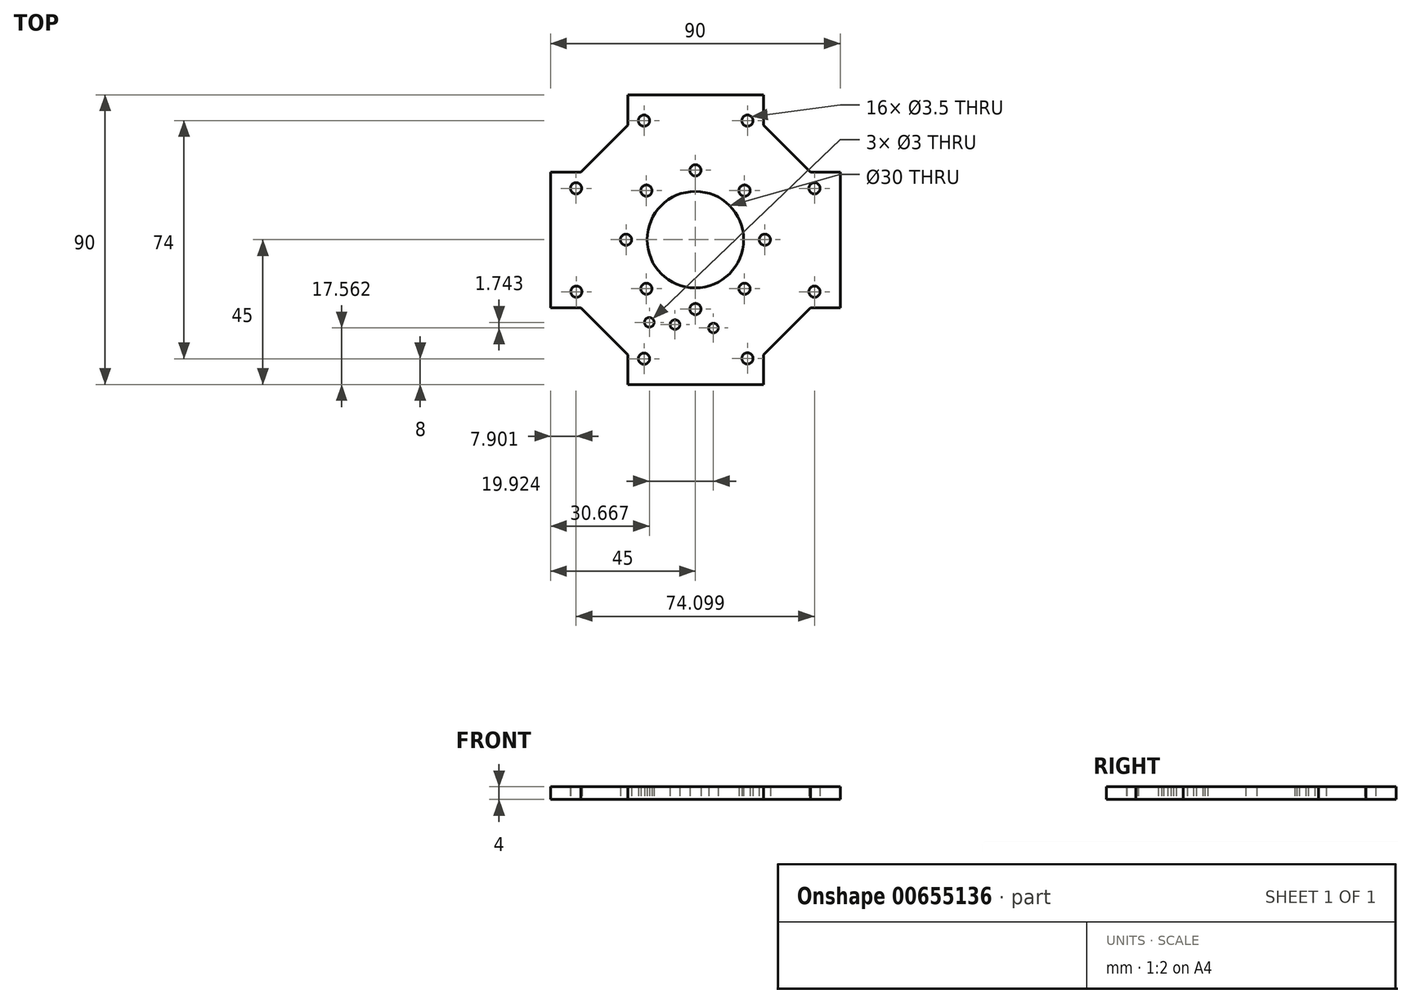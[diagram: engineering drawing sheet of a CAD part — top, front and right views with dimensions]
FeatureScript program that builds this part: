
annotation { "Feature Type Name" : "Feature", "Feature Type Description" : "" }
export const myFeature = defineFeature(function(context is Context, id is Id, definition is map)
    precondition{}
    {
        {
            var Q0;
            Q0=qCreatedBy(makeId("Top.planeOp"),FACE);
            var sketch = newSketch(context, id + "F0", { "sketchPlane" : qUnion([Q0])});
            skLineSegment(sketch, "E0.bottom", {"start": v(24.03, 0) * mm, "end": v(36.03, 0) * mm});
            skLineSegment(sketch, "E0.top", {"start": v(24.03, 90) * mm, "end": v(36.03, 90) * mm});
            skLineSegment(sketch, "E0.left", {"start": v(0, 23.83) * mm, "end": v(0, 35.83) * mm});
            skLineSegment(sketch, "E0.right", {"start": v(90, 23.83) * mm, "end": v(90, 35.83) * mm});
            skLineSegment(sketch, "E1.right", {"start": v(66.17, 80.6) * mm, "end": v(80.8, 65.97) * mm});
            skLineSegment(sketch, "E2", {"start": v(9.4, 65.97) * mm, "end": v(0, 65.97) * mm});
            skLineSegment(sketch, "E3", {"start": v(9.4, 23.83) * mm, "end": v(0, 23.83) * mm});
            skLineSegment(sketch, "E4", {"start": v(24.03, 9.2) * mm, "end": v(24.03, 0) * mm});
            skLineSegment(sketch, "E5", {"start": v(66.17, 9.2) * mm, "end": v(66.17, 0) * mm});
            skLineSegment(sketch, "E6", {"start": v(80.8, 23.83) * mm, "end": v(90, 23.83) * mm});
            skLineSegment(sketch, "E7", {"start": v(80.8, 65.97) * mm, "end": v(90, 65.97) * mm});
            skLineSegment(sketch, "E8", {"start": v(24.03, 80.6) * mm, "end": v(24.03, 90) * mm});
            skLineSegment(sketch, "E9", {"start": v(66.17, 80.6) * mm, "end": v(66.17, 90) * mm});
            skLineSegment(sketch, "E10.trimOffspring", {"start": v(9.4, 23.83) * mm, "end": v(24.03, 9.2) * mm});
            skLineSegment(sketch, "E11.trimOffspring", {"start": v(9.4, 65.97) * mm, "end": v(24.03, 80.6) * mm});
            skPoint(sketch, "E12.orphan", {"position": v(0, 0) * mm});
            skCircle(sketch, "E13", {"center": v(29.03, 82) * mm, "radius": 1.75 * mm});
            skCircle(sketch, "E14", {"center": v(61.17, 82) * mm, "radius": 1.75 * mm});
            skCircle(sketch, "E15", {"center": v(7.9, 60.97) * mm, "radius": 1.75 * mm});
            skCircle(sketch, "E16", {"center": v(8, 28.83) * mm, "radius": 1.75 * mm});
            skCircle(sketch, "E17", {"center": v(82, 28.83) * mm, "radius": 1.75 * mm});
            skCircle(sketch, "E18", {"center": v(29.03, 8) * mm, "radius": 1.75 * mm});
            skCircle(sketch, "E19", {"center": v(61.17, 8.1) * mm, "radius": 1.75 * mm});
            skCircle(sketch, "E20", {"center": v(82, 60.97) * mm, "radius": 1.75 * mm});
            skPoint(sketch, "E21", {"position": v(45, 45) * mm});
            skCircle(sketch, "E22", {"center": v(45, 45) * mm, "radius": 15 * mm});
            skCircle(sketch, "E23", {"center": v(23.43, 45) * mm, "radius": 1.75 * mm});
            skCircle(sketch, "E24", {"center": v(45, 66.57) * mm, "radius": 1.75 * mm});
            skCircle(sketch, "E25", {"center": v(66.57, 45) * mm, "radius": 1.75 * mm});
            skCircle(sketch, "E26", {"center": v(45, 23.43) * mm, "radius": 1.75 * mm});
            skLineSegment(sketch, "E27.trimOffspring", {"start": v(54.17, 90) * mm, "end": v(66.17, 90) * mm});
            skLineSegment(sketch, "E28.trimOffspring", {"start": v(90, 53.97) * mm, "end": v(90, 65.97) * mm});
            skLineSegment(sketch, "E29.trimOffspring", {"start": v(54.17, 0) * mm, "end": v(66.17, 0) * mm});
            skLineSegment(sketch, "E30.trimOffspring", {"start": v(0, 53.97) * mm, "end": v(0, 65.97) * mm});
            skLineSegment(sketch, "E31", {"start": v(66.17, 9.2) * mm, "end": v(80.8, 23.83) * mm});
            skCircle(sketch, "E32", {"center": v(29.75, 60.25) * mm, "radius": 1.75 * mm});
            skCircle(sketch, "E33", {"center": v(29.75, 29.75) * mm, "radius": 1.75 * mm});
            skCircle(sketch, "E34", {"center": v(60.25, 60.25) * mm, "radius": 1.75 * mm});
            skCircle(sketch, "E35", {"center": v(60.25, 29.75) * mm, "radius": 1.75 * mm});
            skLineSegment(sketch, "E36", {"start": v(36.03, 0) * mm, "end": v(54.17, 0) * mm});
            skLineSegment(sketch, "E37", {"start": v(36.03, 90) * mm, "end": v(54.17, 90) * mm});
            skLineSegment(sketch, "E38", {"start": v(0, 53.97) * mm, "end": v(0, 35.83) * mm});
            skLineSegment(sketch, "E39", {"start": v(90, 53.97) * mm, "end": v(90, 35.83) * mm});
            skLineSegment(sketch, "E40", {"start": v(16.72, 16.52) * mm, "end": v(-8.03, -8.23) * mm});
            skLineSegment(sketch, "E41", {"start": v(-8.03, -8.23) * mm, "end": v(-27.83, 11.57) * mm});
            skLineSegment(sketch, "E42", {"start": v(-8.03, -8.23) * mm, "end": v(11.77, -28.03) * mm});
            skLineSegment(sketch, "E43", {"start": v(11.77, -28.03) * mm, "end": v(54.17, 0) * mm});
            skLineSegment(sketch, "E44", {"start": v(-27.83, 11.57) * mm, "end": v(0, 53.97) * mm});
            skLineSegment(sketch, "E45", {"start": v(73.48, 73.28) * mm, "end": v(113.08, 112.88) * mm});
            skLineSegment(sketch, "E46", {"start": v(113.08, 112.88) * mm, "end": v(132.88, 93.08) * mm});
            skLineSegment(sketch, "E47", {"start": v(113.08, 112.88) * mm, "end": v(93.28, 132.68) * mm});
            skLineSegment(sketch, "E48", {"start": v(36.03, 90) * mm, "end": v(93.28, 132.68) * mm});
            skLineSegment(sketch, "E49", {"start": v(132.88, 93.08) * mm, "end": v(90, 35.83) * mm});
            skCircle(sketch, "E50", {"center": v(132.72, -15.48) * mm, "radius": 1.5 * mm});
            skCircle(sketch, "E51", {"center": v(152.72, -15.48) * mm, "radius": 1.5 * mm});
            skLineSegment(sketch, "E52.bottom", {"start": v(147.22, -13.48) * mm, "end": v(147.22, -17.48) * mm});
            skLineSegment(sketch, "E52.top", {"start": v(138.22, -13.48) * mm, "end": v(138.22, -17.48) * mm});
            skLineSegment(sketch, "E52.left", {"start": v(147.22, -13.48) * mm, "end": v(138.22, -13.48) * mm});
            skLineSegment(sketch, "E52.right", {"start": v(147.22, -17.48) * mm, "end": v(138.22, -17.48) * mm});
            skCircle(sketch, "E53", {"center": v(-38.67, -30.86) * mm, "radius": 1.5 * mm});
            skCircle(sketch, "E54", {"center": v(-44.33, -25.2) * mm, "radius": 1.5 * mm});
            skCircle(sketch, "E55", {"center": v(-52.81, -16.72) * mm, "radius": 1.5 * mm});
            skLineSegment(sketch, "E56.0", {"start": v(-44.33, -25.2) * mm, "end": v(-38.67, -30.86) * mm, "construction": true});
            skLineSegment(sketch, "E56.1", {"start": v(-38.67, -30.86) * mm, "end": v(-38.67, -30.86) * mm});
            skLineSegment(sketch, "E56.8", {"start": v(-52.81, -16.72) * mm, "end": v(-44.33, -25.2) * mm, "construction": true});
            skLineSegment(sketch, "E56.9", {"start": v(-44.33, -25.2) * mm, "end": v(-44.33, -25.2) * mm});
            skLineSegment(sketch, "E57.0", {"start": v(-52.81, -16.72) * mm, "end": v(-38.67, -30.86) * mm, "construction": true});
            skCircle(sketch, "E58", {"center": v(30.67, 19.3) * mm, "radius": 1.5 * mm});
            skCircle(sketch, "E59", {"center": v(38.64, 18.6) * mm, "radius": 1.5 * mm});
            skCircle(sketch, "E60", {"center": v(50.6, 17.56) * mm, "radius": 1.5 * mm});
            skLineSegment(sketch, "E61.0", {"start": v(38.64, 18.6) * mm, "end": v(30.67, 19.3) * mm, "construction": true});
            skLineSegment(sketch, "E61.1", {"start": v(45.03, -26.04) * mm, "end": v(45.03, -26.04) * mm});
            skLineSegment(sketch, "E61.8", {"start": v(50.6, 17.56) * mm, "end": v(38.64, 18.6) * mm, "construction": true});
            skLineSegment(sketch, "E61.9", {"start": v(-16.5, -33.99) * mm, "end": v(-16.5, -33.99) * mm});
            skLineSegment(sketch, "E62.0", {"start": v(34.35, 18.98) * mm, "end": v(30.67, 19.3) * mm, "construction": true});
            skCircle(sketch, "E63", {"center": v(-1.87, -7.98) * mm, "radius": 1.5 * mm});
            skCircle(sketch, "E64", {"center": v(12.27, -22.13) * mm, "radius": 1.5 * mm});
            skLineSegment(sketch, "E65.bottom", {"start": v(9.8, -16.82) * mm, "end": v(6.97, -19.65) * mm});
            skLineSegment(sketch, "E65.top", {"start": v(3.43, -10.46) * mm, "end": v(0.6, -13.29) * mm});
            skLineSegment(sketch, "E65.left", {"start": v(9.8, -16.82) * mm, "end": v(3.43, -10.46) * mm});
            skLineSegment(sketch, "E65.right", {"start": v(6.97, -19.65) * mm, "end": v(0.6, -13.29) * mm});
            skLineSegment(sketch, "E66.0", {"start": v(0.6, -13.29) * mm, "end": v(6.97, -19.65) * mm, "construction": true});
            skLineSegment(sketch, "E66.1", {"start": v(6.97, -19.65) * mm, "end": v(6.97, -19.65) * mm});
            skLineSegment(sketch, "E66.8", {"start": v(-1.87, -7.98) * mm, "end": v(12.27, -22.13) * mm, "construction": true});
            skLineSegment(sketch, "E66.9", {"start": v(12.27, -22.13) * mm, "end": v(12.27, -22.13) * mm});
            skSolve(sketch);
        }
        {
            var Q0;
            Q0=makeQuery(id+"F0.imprint","IMPRINT",FACE,{"disambiguationData":[TD([[makeQuery(id+"F0.imprint","IMPRINT",EDGE,{"derivedFrom":sQuery(id+"F0.wireOp",EDGE,"E0.bottom")}),1.0]])]});
            extrude(context, id + "F1", {"entities" : qUnion([Q0]), "depth" : 4 * mm, "offsetDistance" : 25 * mm});
        }
    });
